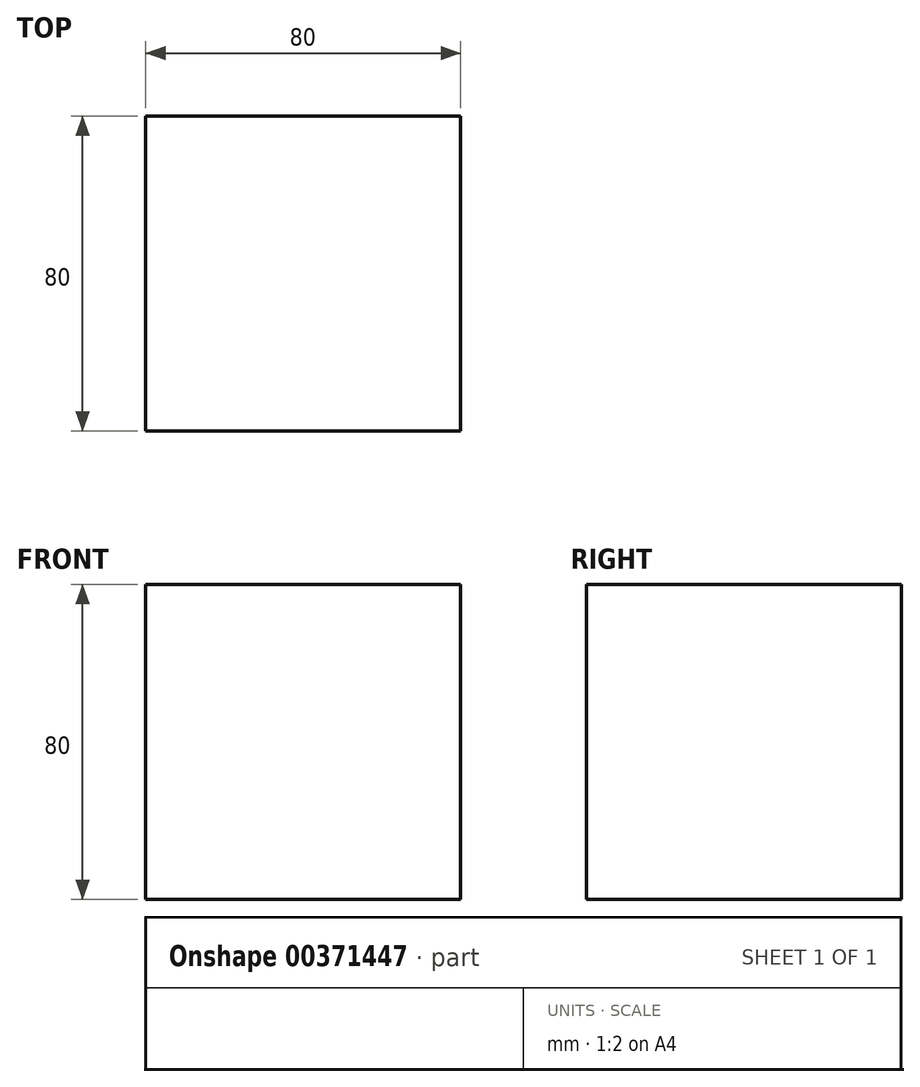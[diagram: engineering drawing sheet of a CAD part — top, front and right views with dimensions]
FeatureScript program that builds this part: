
annotation { "Feature Type Name" : "Feature", "Feature Type Description" : "" }
export const myFeature = defineFeature(function(context is Context, id is Id, definition is map)
    precondition{}
    {
        {
            var Q0;
            Q0=qCreatedBy(makeId("Top.planeOp"),FACE);
            var sketch = newSketch(context, id + "F0", { "sketchPlane" : qUnion([Q0])});
            skLineSegment(sketch, "E0.bottom", {"start": v(-80, 97) * mm, "end": v(0, 97) * mm});
            skLineSegment(sketch, "E0.top", {"start": v(-80, 17) * mm, "end": v(0, 17) * mm});
            skLineSegment(sketch, "E0.left", {"start": v(-80, 97) * mm, "end": v(-80, 17) * mm});
            skLineSegment(sketch, "E0.right", {"start": v(0, 97) * mm, "end": v(0, 17) * mm});
            skSolve(sketch);
        }
        {
            var Q0;
            Q0=makeQuery(id+"F0.imprint","IMPRINT",FACE,{"disambiguationData":[TD([[makeQuery(id+"F0.imprint","IMPRINT",EDGE,{"derivedFrom":sQuery(id+"F0.wireOp",EDGE,"E0.bottom")}),-1.0]])]});
            extrude(context, id + "F1", {"entities" : qUnion([Q0]), "depth" : 80 * mm});
        }
    });
